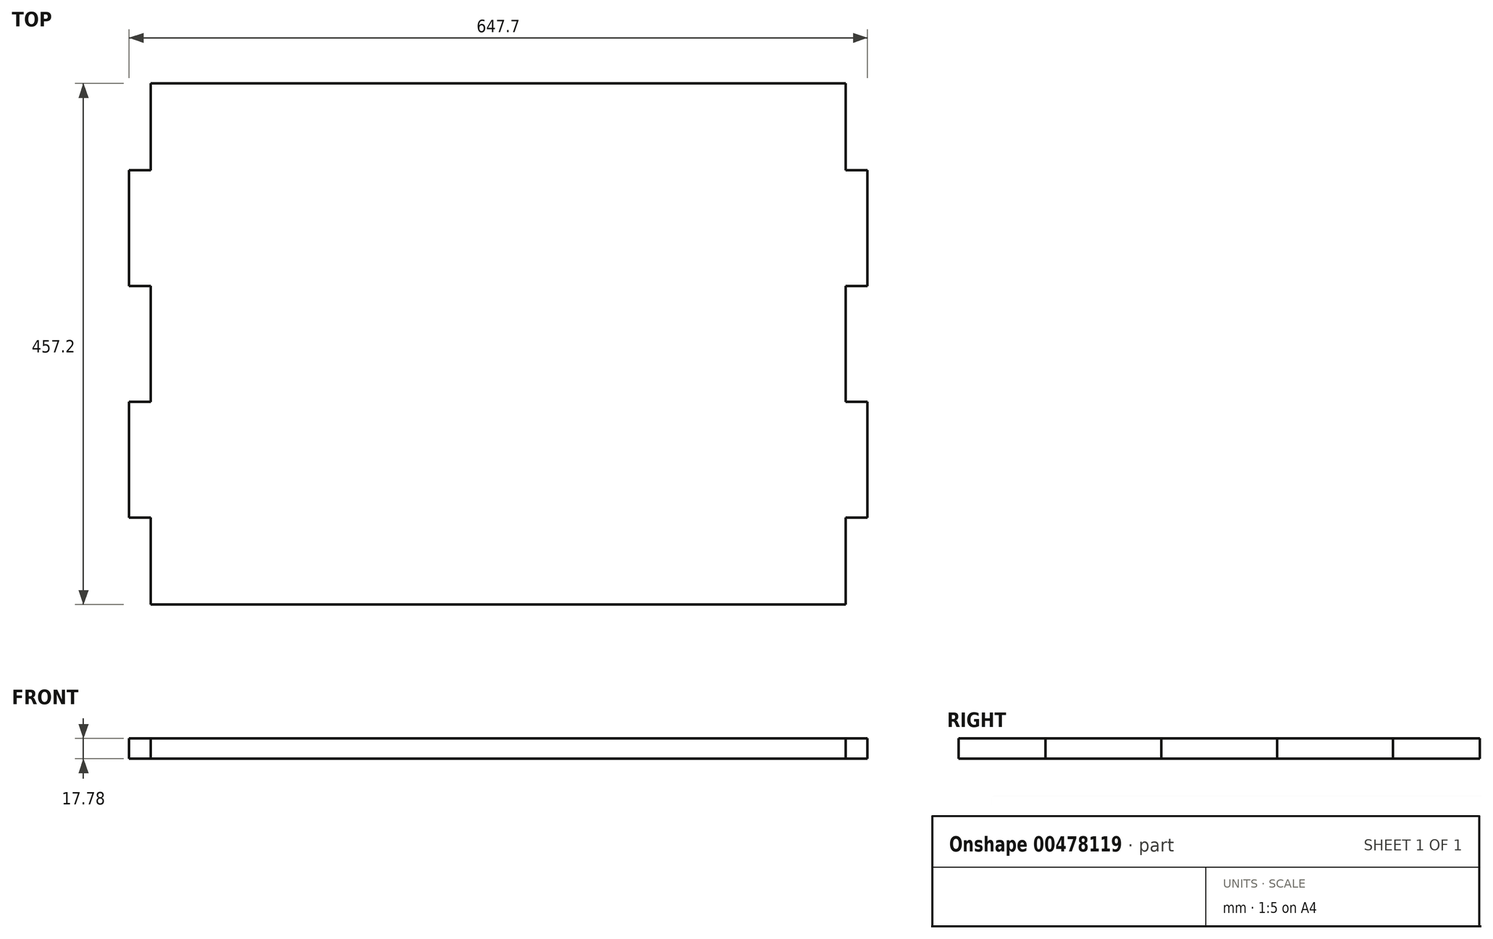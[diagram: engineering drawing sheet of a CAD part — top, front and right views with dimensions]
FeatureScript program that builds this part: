
annotation { "Feature Type Name" : "Feature", "Feature Type Description" : "" }
export const myFeature = defineFeature(function(context is Context, id is Id, definition is map)
    precondition{}
    {
        {
            var Q0;
            Q0=qCreatedBy(makeId("Top.planeOp"),FACE);
            var sketch = newSketch(context, id + "F0", { "sketchPlane" : qUnion([Q0])});
            skPoint(sketch, "E0.middle", {"position": v(0, 0) * mm});
            skLineSegment(sketch, "E1", {"start": v(0, 0) * mm, "end": v(0, -76.2) * mm});
            skLineSegment(sketch, "E2", {"start": v(0, -76.2) * mm, "end": v(-19.05, -76.2) * mm});
            skLineSegment(sketch, "E3", {"start": v(-19.05, -76.2) * mm, "end": v(-19.05, -177.8) * mm});
            skLineSegment(sketch, "E4", {"start": v(-19.05, -177.8) * mm, "end": v(0, -177.8) * mm});
            skLineSegment(sketch, "E5", {"start": v(0, -177.8) * mm, "end": v(0, -279.4) * mm});
            skLineSegment(sketch, "E6", {"start": v(0, -279.4) * mm, "end": v(-19.05, -279.4) * mm});
            skLineSegment(sketch, "E7", {"start": v(-19.05, -279.4) * mm, "end": v(-19.05, -381) * mm});
            skLineSegment(sketch, "E8", {"start": v(-19.05, -381) * mm, "end": v(0, -381) * mm});
            skLineSegment(sketch, "E9", {"start": v(0, -381) * mm, "end": v(0, -457.2) * mm});
            skLineSegment(sketch, "E10", {"start": v(0, 0) * mm, "end": v(609.6, 0) * mm});
            skLineSegment(sketch, "E11", {"start": v(609.6, 0) * mm, "end": v(609.6, -76.2) * mm});
            skLineSegment(sketch, "E12", {"start": v(609.6, -76.2) * mm, "end": v(628.65, -76.2) * mm});
            skLineSegment(sketch, "E13", {"start": v(628.65, -76.2) * mm, "end": v(628.65, -177.8) * mm});
            skLineSegment(sketch, "E14", {"start": v(628.65, -177.8) * mm, "end": v(609.6, -177.8) * mm});
            skLineSegment(sketch, "E15", {"start": v(609.6, -177.8) * mm, "end": v(609.6, -279.4) * mm});
            skLineSegment(sketch, "E16", {"start": v(609.6, -279.4) * mm, "end": v(628.65, -279.4) * mm});
            skLineSegment(sketch, "E17", {"start": v(628.65, -279.4) * mm, "end": v(628.65, -381) * mm});
            skLineSegment(sketch, "E18", {"start": v(628.65, -381) * mm, "end": v(609.6, -381) * mm});
            skLineSegment(sketch, "E19", {"start": v(609.6, -381) * mm, "end": v(609.6, -457.2) * mm});
            skLineSegment(sketch, "E20", {"start": v(609.6, -457.2) * mm, "end": v(0, -457.2) * mm});
            skSolve(sketch);
        }
        {
            var Q0;
            Q0=makeQuery(id+"F0.imprint","IMPRINT",FACE,{"disambiguationData":[TD([[makeQuery(id+"F0.imprint","IMPRINT",EDGE,{"derivedFrom":sQuery(id+"F0.wireOp",EDGE,"E1")}),1.0]])]});
            extrude(context, id + "F1", {"entities" : qUnion([Q0]), "depth" : 17.78 * mm});
        }
    });
